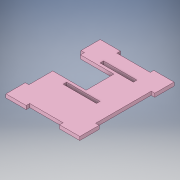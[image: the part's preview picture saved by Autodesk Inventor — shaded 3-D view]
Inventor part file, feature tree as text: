
AUTODESK INVENTOR PART (.ipt)
format: ipt  version: 2019 (Build 230136000, 136)  size: 158,208 bytes
history: native  units: mm
features: extrude x1, sketch x1
ambient origin geometry x8: Origin, YZ Plane, XZ Plane, XY Plane, X Axis, Y Axis, Z Axis, Center Point
bodies: Body1 (feature_tree)
feature tree (2):
  extrude  "Extrusión2"  Depth=66.36mm
  sketch  "Boceto2"  dims[d37=84.72mm d38=66.36mm d39=30.0mm d40=3.18mm d41=0.0mm d42=3.18mm d43=30.0mm d44=30.0mm d45=3.18mm d46=30.0mm d47=30.0mm d48=12.0mm d49=50.0mm d50=0.0mm d51=0.0mm d52=50.0mm d53=15.0mm d54=25.0mm d57=3.18mm d58=0.0mm d59=30.0mm]
